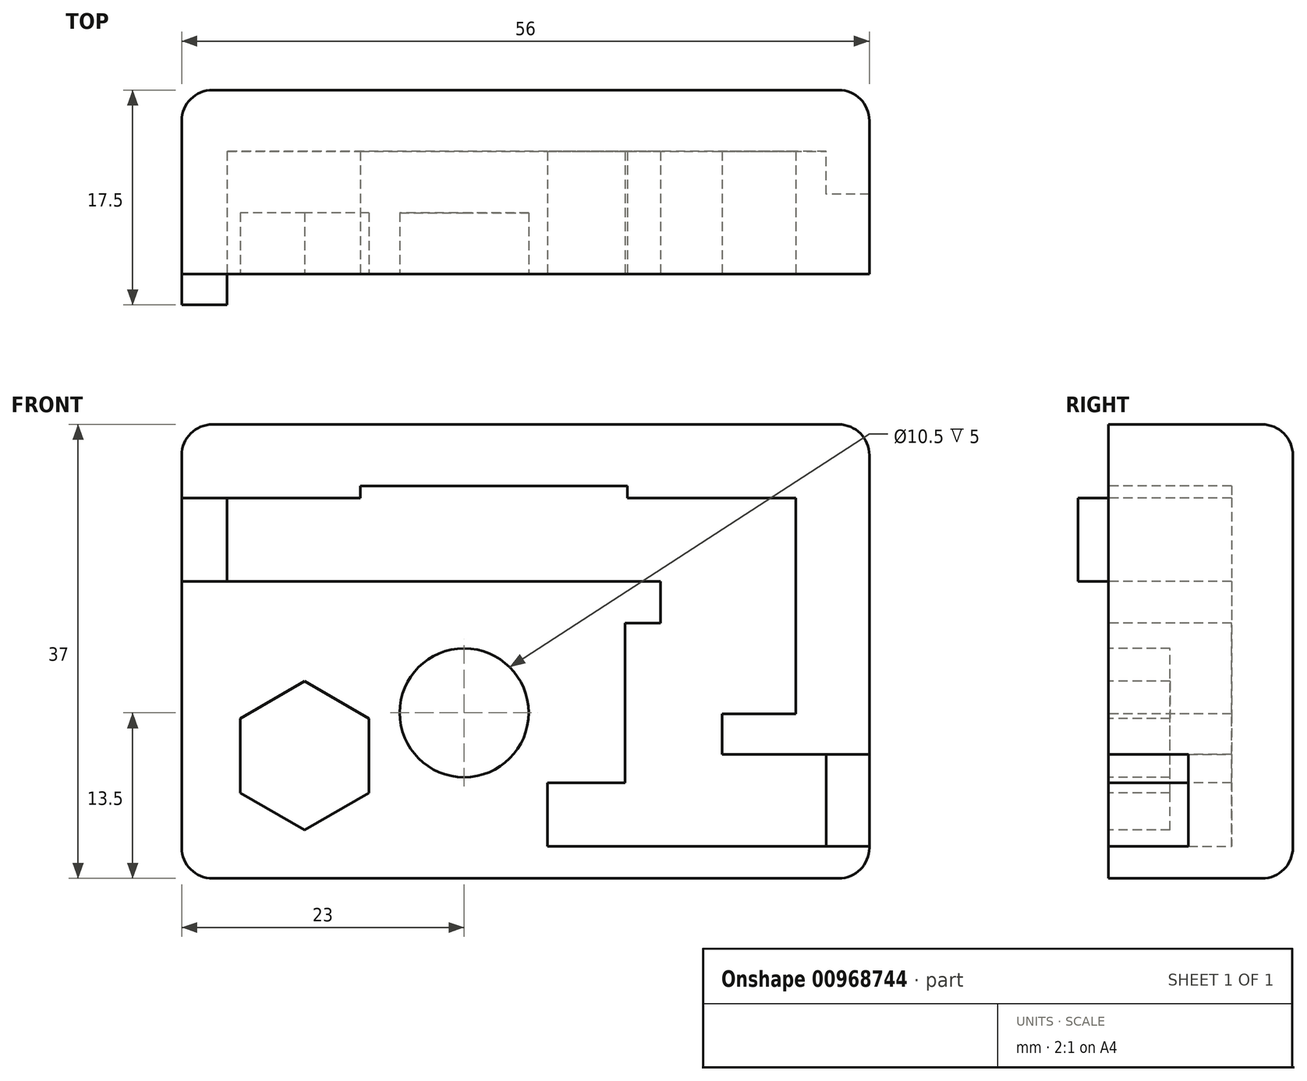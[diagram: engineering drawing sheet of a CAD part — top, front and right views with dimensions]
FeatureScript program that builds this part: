
annotation { "Feature Type Name" : "Feature", "Feature Type Description" : "" }
export const myFeature = defineFeature(function(context is Context, id is Id, definition is map)
    precondition{}
    {
        {
            var Q0;
            Q0=qCreatedBy(makeId("Front.planeOp"),FACE);
            var sketch = newSketch(context, id + "F0", { "sketchPlane" : qUnion([Q0])});
            skLineSegment(sketch, "E0.bottom", {"start": v(-28, 18.5) * mm, "end": v(28, 18.5) * mm});
            skLineSegment(sketch, "E0.top", {"start": v(-28, -18.5) * mm, "end": v(28, -18.5) * mm});
            skLineSegment(sketch, "E0.left", {"start": v(-28, 18.5) * mm, "end": v(-28, -18.5) * mm});
            skLineSegment(sketch, "E0.right", {"start": v(28, 18.5) * mm, "end": v(28, -18.5) * mm});
            skSolve(sketch);
        }
        {
            var Q0;
            Q0 = qSketchRegion(id + "F0", true);
            extrude(context, id + "F1", {"entities" : qUnion([Q0]), "oppositeDirection" : true, "depth" : 15 * mm, "offsetDistance" : 25 * mm});
        }
        {
            var Q0;
            Q0=makeQuery(id+"F1.opExtrude","CAP_FACE",FACE,{"disambiguationData":[OSD([sQuery(id+"F0.wireOp",EDGE,"E0.bottom"),sQuery(id+"F0.wireOp",EDGE,"E0.top"),sQuery(id+"F0.wireOp",EDGE,"E0.left"),sQuery(id+"F0.wireOp",EDGE,"E0.right")])],"isStart":true});
            var sketch = newSketch(context, id + "F2", { "sketchPlane" : qUnion([Q0])});
            skLineSegment(sketch, "E1", {"start": v(-24.3, 12.5) * mm, "end": v(-13.47, 12.5) * mm});
            skLineSegment(sketch, "E2", {"start": v(22, 12.5) * mm, "end": v(22, -5.1) * mm});
            skLineSegment(sketch, "E3", {"start": v(22, -5.1) * mm, "end": v(16, -5.1) * mm});
            skLineSegment(sketch, "E4", {"start": v(16, -5.1) * mm, "end": v(16, -8.4) * mm});
            skLineSegment(sketch, "E5", {"start": v(16, -8.4) * mm, "end": v(28, -8.4) * mm});
            skLineSegment(sketch, "E6", {"start": v(28, -8.4) * mm, "end": v(28, -15.9) * mm});
            skLineSegment(sketch, "E7", {"start": v(28, -15.9) * mm, "end": v(1.8, -15.9) * mm});
            skLineSegment(sketch, "E8", {"start": v(1.8, -15.9) * mm, "end": v(1.8, -10.7) * mm});
            skLineSegment(sketch, "E9", {"start": v(1.8, -10.7) * mm, "end": v(8.1, -10.7) * mm});
            skLineSegment(sketch, "E10", {"start": v(8.1, -10.7) * mm, "end": v(8.1, 2.3) * mm});
            skLineSegment(sketch, "E11", {"start": v(8.1, 2.3) * mm, "end": v(11, 2.3) * mm});
            skLineSegment(sketch, "E12", {"start": v(11, 5.7) * mm, "end": v(-24.3, 5.7) * mm});
            skLineSegment(sketch, "E13", {"start": v(-24.3, 12.5) * mm, "end": v(-24.3, 5.7) * mm});
            skLineSegment(sketch, "E14", {"start": v(-9.04, 13.5) * mm, "end": v(8.3, 13.5) * mm});
            skLineSegment(sketch, "E15", {"start": v(8.3, 13.5) * mm, "end": v(8.3, 12.5) * mm});
            skLineSegment(sketch, "E16", {"start": v(-13.47, 12.5) * mm, "end": v(-13.47, 13.5) * mm});
            skLineSegment(sketch, "E17", {"start": v(-13.47, 13.5) * mm, "end": v(-9.04, 13.5) * mm});
            skLineSegment(sketch, "E18.trimOffspring", {"start": v(8.3, 12.5) * mm, "end": v(22, 12.5) * mm});
            skLineSegment(sketch, "E19", {"start": v(11, 5.7) * mm, "end": v(11, 2.3) * mm});
            skSolve(sketch);
        }
        {
            var Q0;
            Q0 = qSketchRegion(id + "F2", true);
            extrude(context, id + "F3", {"entities" : qUnion([Q0]), "operationType" : NewBodyOperationType.REMOVE, "oppositeDirection" : true, "depth" : 10 * mm, "offsetDistance" : 25 * mm});
        }
        {
            var Q0;
            Q0=makeQuery(id+"F1.opExtrude","CAP_FACE",FACE,{"disambiguationData":[OSD([sQuery(id+"F0.wireOp",EDGE,"E0.bottom"),sQuery(id+"F0.wireOp",EDGE,"E0.top"),sQuery(id+"F0.wireOp",EDGE,"E0.left"),sQuery(id+"F0.wireOp",EDGE,"E0.right")])],"isStart":true});
            var sketch = newSketch(context, id + "F4", { "sketchPlane" : qUnion([Q0])});
            skLineSegment(sketch, "E20.bottom", {"start": v(-24.3, 12.5) * mm, "end": v(-28, 12.5) * mm});
            skLineSegment(sketch, "E20.top", {"start": v(-24.3, 5.7) * mm, "end": v(-28, 5.7) * mm});
            skLineSegment(sketch, "E20.left", {"start": v(-24.3, 12.5) * mm, "end": v(-24.3, 5.7) * mm});
            skLineSegment(sketch, "E20.right", {"start": v(-28, 12.5) * mm, "end": v(-28, 5.7) * mm});
            skSolve(sketch);
        }
        {
            var Q0;
            Q0 = qSketchRegion(id + "F4", true);
            extrude(context, id + "F5", {"entities" : qUnion([Q0]), "operationType" : NewBodyOperationType.ADD, "depth" : 2.5 * mm, "offsetDistance" : 25 * mm});
        }
        {
            var Q0;
            {var subQ0=sQuery(id+"F0.wireOp",EDGE,"E0.left");var subQ1=sQuery(id+"F0.wireOp",EDGE,"E0.bottom");var subQ2=sQuery(id+"F0.wireOp",EDGE,"E0.right");Q0=makeQuery(id+"F5.boolean.opBoolean","SPLIT",FACE,{"disambiguationData":[TD([makeQuery(id+"F1.opExtrude","SWEPT_FACE",FACE,{"disambiguationData":[OSD([subQ1])]})])],"derivedFrom":makeQuery(id+"F1.opExtrude","CAP_FACE",FACE,{"disambiguationData":[OSD([subQ1,sQuery(id+"F0.wireOp",EDGE,"E0.top"),subQ0,subQ2])],"isStart":true})});}
            var sketch = newSketch(context, id + "F6", { "sketchPlane" : qUnion([Q0])});
            skCircle(sketch, "E21.cCircle", {"center": v(-18, -8.5) * mm, "radius": 5.25 * mm, "construction": true});
            skLineSegment(sketch, "E21.0", {"start": v(-23.25, -11.53) * mm, "end": v(-23.25, -5.47) * mm});
            skLineSegment(sketch, "E21.1", {"start": v(-23.25, -5.47) * mm, "end": v(-18, -2.44) * mm});
            skLineSegment(sketch, "E21.2", {"start": v(-18, -2.44) * mm, "end": v(-12.75, -5.47) * mm});
            skLineSegment(sketch, "E21.3", {"start": v(-12.75, -5.47) * mm, "end": v(-12.75, -11.53) * mm});
            skLineSegment(sketch, "E21.4", {"start": v(-12.75, -11.53) * mm, "end": v(-18, -14.56) * mm});
            skLineSegment(sketch, "E21.5", {"start": v(-18, -14.56) * mm, "end": v(-23.25, -11.53) * mm});
            skPoint(sketch, "E21.0.midPoint", {"position": v(-23.25, -8.5) * mm});
            skSolve(sketch);
        }
        {
            var Q0;
            Q0 = qSketchRegion(id + "F6", true);
            extrude(context, id + "F7", {"entities" : qUnion([Q0]), "operationType" : NewBodyOperationType.REMOVE, "oppositeDirection" : true, "depth" : 5 * mm, "offsetDistance" : 25 * mm});
        }
        {
            var Q0;
            Q0=makeQuery(id+"F3.boolean.opBoolean","COPY",FACE,{"derivedFrom":makeQuery(id+"F3.opExtrude","CAP_FACE",FACE,{"disambiguationData":[OSD([sQuery(id+"F2.wireOp",EDGE,"E1"),sQuery(id+"F2.wireOp",EDGE,"E2"),sQuery(id+"F2.wireOp",EDGE,"E3"),sQuery(id+"F2.wireOp",EDGE,"E4"),sQuery(id+"F2.wireOp",EDGE,"E5"),sQuery(id+"F2.wireOp",EDGE,"E6"),sQuery(id+"F2.wireOp",EDGE,"E7"),sQuery(id+"F2.wireOp",EDGE,"E8"),sQuery(id+"F2.wireOp",EDGE,"E9"),sQuery(id+"F2.wireOp",EDGE,"E10"),sQuery(id+"F2.wireOp",EDGE,"E11"),sQuery(id+"F2.wireOp",EDGE,"E12"),sQuery(id+"F2.wireOp",EDGE,"E13"),sQuery(id+"F2.wireOp",EDGE,"E14"),sQuery(id+"F2.wireOp",EDGE,"E15"),sQuery(id+"F2.wireOp",EDGE,"E16"),sQuery(id+"F2.wireOp",EDGE,"E17"),sQuery(id+"F2.wireOp",EDGE,"E18.trimOffspring"),sQuery(id+"F2.wireOp",EDGE,"E19")])],"isStart":false})});
            var sketch = newSketch(context, id + "F8", { "sketchPlane" : qUnion([Q0])});
            skLineSegment(sketch, "E22.bottom", {"start": v(28, -8.4) * mm, "end": v(24.5, -8.4) * mm});
            skLineSegment(sketch, "E22.top", {"start": v(28, -15.9) * mm, "end": v(24.5, -15.9) * mm});
            skLineSegment(sketch, "E22.left", {"start": v(28, -8.4) * mm, "end": v(28, -15.9) * mm});
            skLineSegment(sketch, "E22.right", {"start": v(24.5, -8.4) * mm, "end": v(24.5, -15.9) * mm});
            skSolve(sketch);
        }
        {
            var Q0;
            Q0 = qSketchRegion(id + "F8", true);
            extrude(context, id + "F9", {"entities" : qUnion([Q0]), "operationType" : NewBodyOperationType.ADD, "depth" : 3.5 * mm, "offsetDistance" : 25 * mm});
        }
        {
            var Q0;
            Q0=makeQuery(id+"F1.opExtrude","SWEPT_EDGE",EDGE,{"disambiguationData":[OSD([sQuery(id+"F0.wireOp",EDGE,"E0.top"),sQuery(id+"F0.wireOp",EDGE,"E0.right")])]});
            var Q1;
            Q1=makeQuery(id+"F1.opExtrude","SWEPT_EDGE",EDGE,{"disambiguationData":[OSD([sQuery(id+"F0.wireOp",EDGE,"E0.bottom"),sQuery(id+"F0.wireOp",EDGE,"E0.right")])]});
            var Q2;
            Q2=makeQuery(id+"F1.opExtrude","SWEPT_EDGE",EDGE,{"disambiguationData":[OSD([sQuery(id+"F0.wireOp",EDGE,"E0.bottom"),sQuery(id+"F0.wireOp",EDGE,"E0.left")])]});
            var Q3;
            Q3=makeQuery(id+"F1.opExtrude","SWEPT_EDGE",EDGE,{"disambiguationData":[OSD([sQuery(id+"F0.wireOp",EDGE,"E0.top"),sQuery(id+"F0.wireOp",EDGE,"E0.left")])]});
            var Q4;
            Q4=makeQuery(id+"F1.opExtrude","CAP_EDGE",EDGE,{"disambiguationData":[OSD([sQuery(id+"F0.wireOp",EDGE,"E0.right")])],"isStart":false});
            var Q5;
            Q5=makeQuery(id+"F1.opExtrude","CAP_EDGE",EDGE,{"disambiguationData":[OSD([sQuery(id+"F0.wireOp",EDGE,"E0.bottom")])],"isStart":false});
            var Q6;
            Q6=makeQuery(id+"F1.opExtrude","CAP_EDGE",EDGE,{"disambiguationData":[OSD([sQuery(id+"F0.wireOp",EDGE,"E0.top")])],"isStart":false});
            var Q7;
            Q7=makeQuery(id+"F1.opExtrude","CAP_EDGE",EDGE,{"disambiguationData":[OSD([sQuery(id+"F0.wireOp",EDGE,"E0.left")])],"isStart":false});
            fillet(context, id + "F10", {"entities" : qUnion([Q0, Q1, Q2, Q3, Q4, Q5, Q6, Q7]), "radius" : 2.5 * mm, "tangentPropagation" : true, "allowEdgeOverflow" : false});
        }
        {
            var Q0;
            {var subQ0=sQuery(id+"F0.wireOp",EDGE,"E0.top");var subQ1=sQuery(id+"F0.wireOp",EDGE,"E0.left");var subQ2=sQuery(id+"F0.wireOp",EDGE,"E0.right");Q0=makeQuery(id+"F5.boolean.opBoolean","SPLIT",FACE,{"disambiguationData":[TD([makeQuery(id+"F1.opExtrude","SWEPT_FACE",FACE,{"disambiguationData":[OSD([subQ0])]})])],"derivedFrom":makeQuery(id+"F1.opExtrude","CAP_FACE",FACE,{"disambiguationData":[OSD([sQuery(id+"F0.wireOp",EDGE,"E0.bottom"),subQ0,subQ1,subQ2])],"isStart":true})});}
            var sketch = newSketch(context, id + "F11", { "sketchPlane" : qUnion([Q0])});
            skCircle(sketch, "E23", {"center": v(-5, -5) * mm, "radius": 5.25 * mm});
            skSolve(sketch);
        }
        {
            var Q0;
            Q0 = qSketchRegion(id + "F11", true);
            extrude(context, id + "F12", {"entities" : qUnion([Q0]), "operationType" : NewBodyOperationType.REMOVE, "oppositeDirection" : true, "depth" : 5 * mm, "offsetDistance" : 25 * mm});
        }
    });
